# Revit family: Fireplaces_DaVinci_TimberFyre_48x30-SS-TF
name_source: partatom
category: Mechanical Equipment
units: mm (PartAtom-declared; Revit-internal decimal feet)

## family parameters
Always vertical = Yes
Cut with Voids When Loaded = Yes
Maintain Annotation Orientation = No
OmniClass Number = 23.75.00.00
OmniClass Title = Climate Control (HVAC)
Part Type = Normal
Room Calculation Point = No
Round Connector Dimension = Use Diameter
Shared = No
Work Plane-Based = Yes

## types (1)
- Timberfyre Signle Sided 48" x 30"
    Apparent Load = 0 VA
    CAD Details = https://www.arcat.com
    Cost = 0 $
    Default Elevation = 48"
    Depth = 24"
    Electrical Req'd = 120 V
    Exhaust = 8"
    Gas Req'd = 115,000 BTU's
    Glass = Glass
    Height = 60 5/8"
    Intakes = 6"
    LP = Min = 11"wc (2.74 kpa), Max = 13"wc (3.23 kpa)
    Manufacturer = Davinci Custom Fireplaces
    Matel = Matel
    Model = Timberfyre Signle Sided 48" x 30"
    NG = Min = 5.5"wc (1.37kpa), Max = 7"wc (1.74 kpa)
    Number Pole = 1
    Product Documentation Link = https://www.travisindustries.com
    Product Page URL = https://www.arcat.com
    Specifications = https://www.arcat.com
    URL = https://www.davincifireplace.com
    Width = 50"
    X1 = 8 1/2"
    X2 = 6 1/2"

## geometry (parser evidence)
native form markers: Sweep x2
no freeform markers — native parametric forms only
